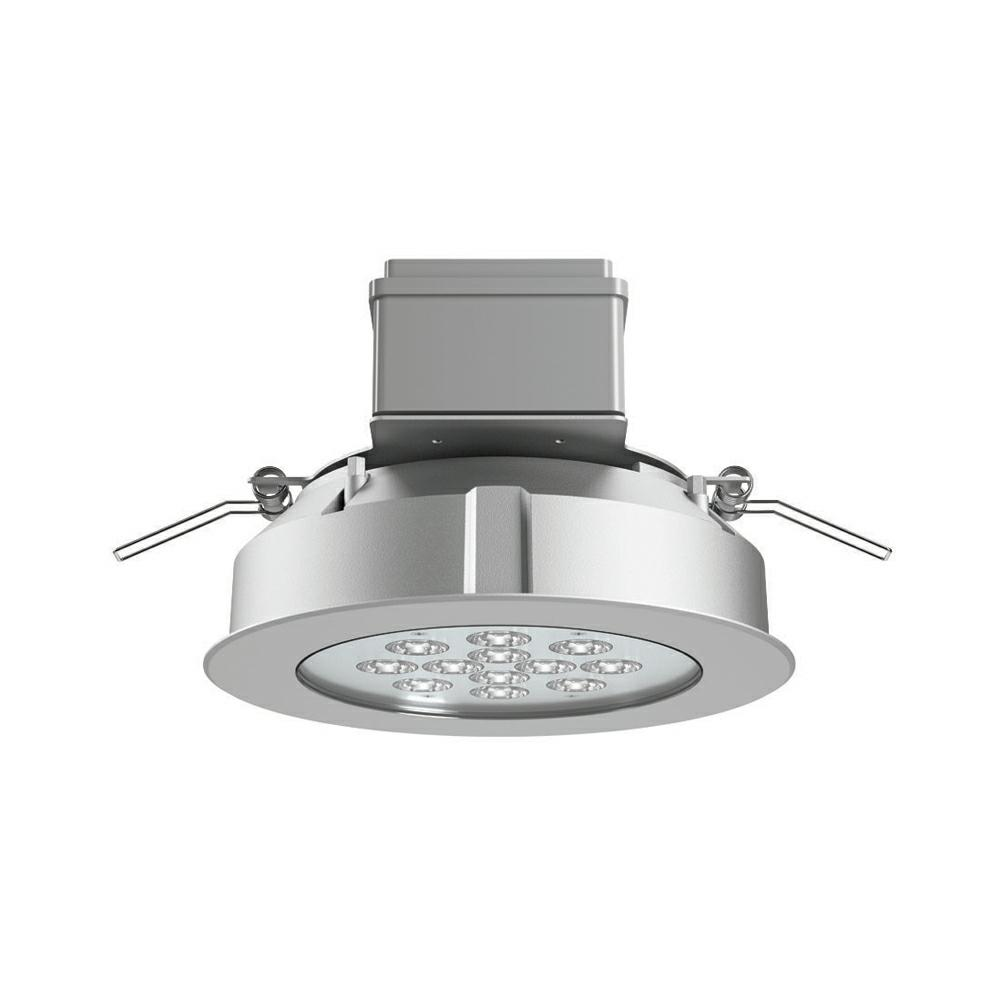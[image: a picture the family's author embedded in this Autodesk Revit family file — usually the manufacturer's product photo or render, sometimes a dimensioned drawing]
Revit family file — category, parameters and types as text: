
# Revit family: Platek_Oblò_Ceiling Recessed
name_source: partatom
category: Apparecchi per illuminazione
revit_build: Autodesk Revit 2017 (Build: 20160225_1515(x64)
units: mm (PartAtom-declared; Revit-internal decimal feet)

## family parameters
Condiviso = No
Host = Superficie
Punto di calcolo locali = No
Quota connettore circolare = Usa diametro
Sorgente d'illuminazione = Sì
Taglio con vuoti quando caricato = No
Tipo di parte = Normale

## types (5) — shared parameters
Angolo inclinazione = -90.00°
Body = PLK_Aluminium
CRI = >80
Colour Temperature = 3000 K
Commenti sul tipo = Balconies, Facades
Current = 0 A
Descrizione = Outdoor Lighting, Ceiling Recessed
Diffuse Type = 8mm flat tempered extra clear gass
Dimmable = NO
Emetti da diametro cerchio = 146 mm
Energy Efficiency Rating = A/A+/A++
Filtro dei colori = 16777215
Frequency = 50/60Hz
Insulation Class = 2
LED Protection = Surge Protection Included
Light Source = PLK_Light Source
Manufacturer Comment = Aluminium Body
Modello = Oblò Ceiling Recessed
Mounting Type = Ceiling  Recessed
Nota chiave = Other Led colors available on request
PLATEK FInishes = Aluminium
Power Supply Unit = Power Supply Included
Product Dimension = Ø 210mm/H 127mm
Product Documentation Link = http://www.platek.eu
Product Page URL = http://www.platek.eu
Produttore = PLATEK SRL
Prospetto di default = 1219 mm
Rendi la forma visibile nel rendering = No
Supply Voltage = 220 V
Supply Voltage Max = 240 V
Supply Voltage Min = 220 V
URL = www.platek.eu
Variazione temperatura colore lampada con luminosità attenuata = <Nessuno>

## per-type parameters (varying)
| type | Beam Angle | Cable Lenght | File diagramma fotometrico | IK Rating | IP Rating | Immagine tipo | L | Lampada | Luminaire Luminous Flux | Luminaire Luminous Intensity | Luminaire Wattage | PLATEK Article Code |
| 8488411_21W_LED_3000K_Ceiling Recessed | 9.00° | 0,5 m | 8488411.IES | IK 08 | IP 65 | oblo_incasso_soffitto.jpg | Sì | LED | 1935 lm | 39996 cd | 21 W | 8488411 |
| 8488413_21W_LED_3000K_Ceiling Recessed | 28.00° | 0,5 m | 8488413.IES | IK 08 | IP 65 | oblo_incasso_soffitto.jpg | Sì | LED | 1810 lm | 8752 cd | 21 W | 8488413 |
| 8488418_21W_LED_3000K_Ceiling Recessed | 45.00° | 0,5 m | 8488418.IES | IK08 | IP65 | oblo_incasso_soffitto.jpg | Sì | LED | 1615 lm | 1614 cd | 21 W | 8488418 |
| 8488518_18,5W_LED_3000K_Ceiling Recessed | 108.00° | 0,5m | 8488518.IES | IK08 | IP65 | oblo_cob_incasso_soffitto.jpg | No | COB LED | 1910 lm | 860 cd | 19 W | 8488518 |
| 8488718_27W_LED_3000K_Ceiling Recessed | 108.00° | 0,5m | 8488718.IES | IK08 | IP68 Full dry | oblo_cob_incasso_soffitto.jpg | No | COB LED | 2700 lm | 906 cd | 27 W | 8488718 |
